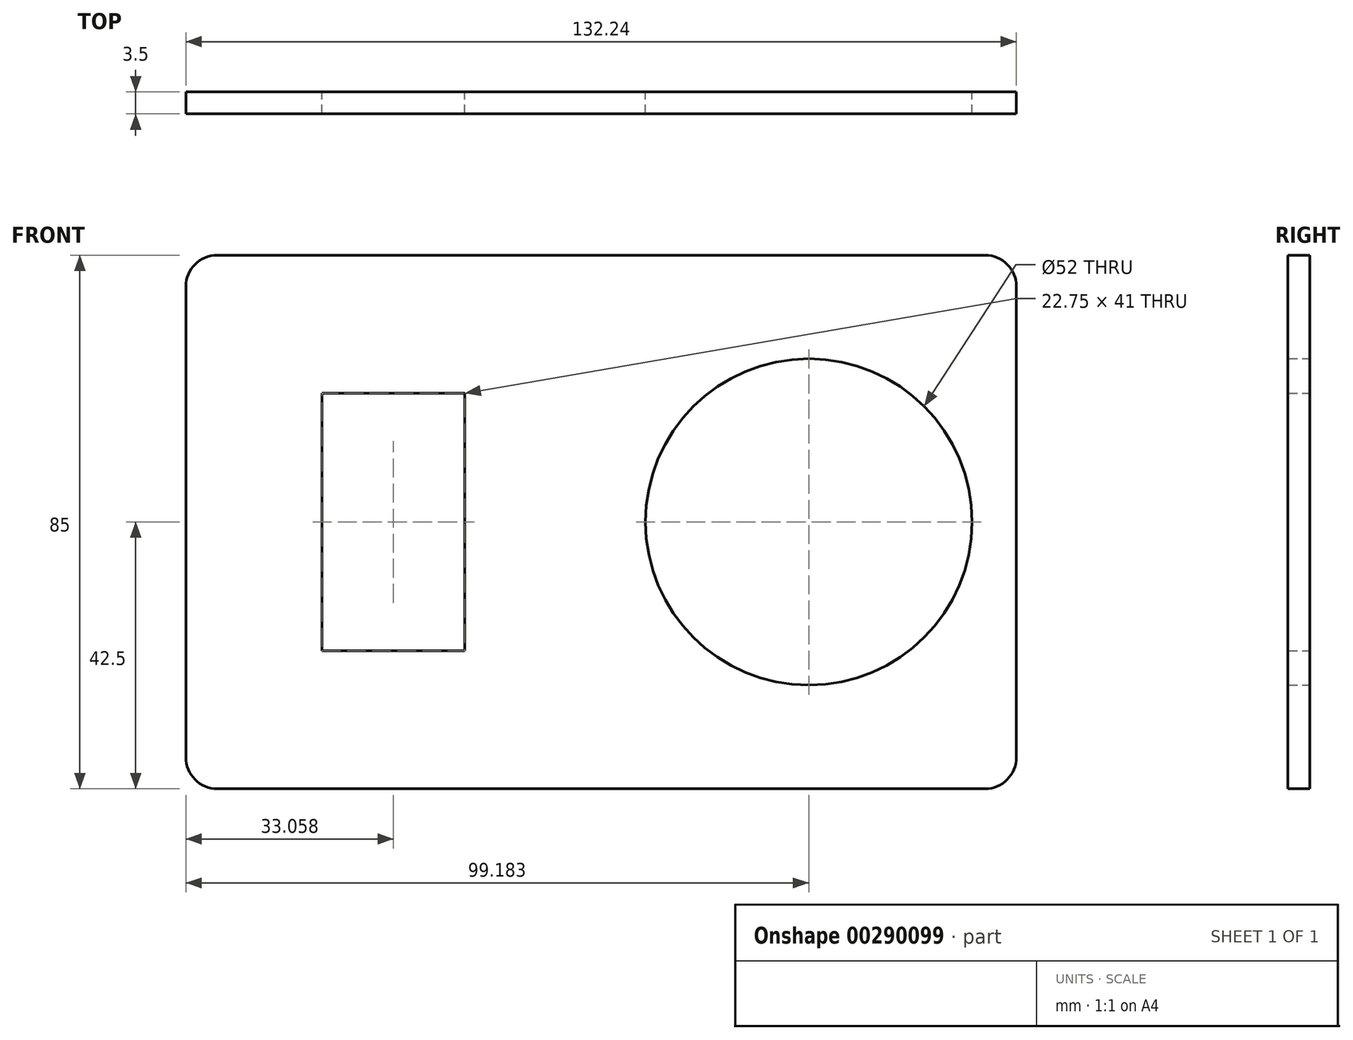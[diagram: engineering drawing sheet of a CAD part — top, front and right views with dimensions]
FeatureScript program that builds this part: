
annotation { "Feature Type Name" : "Feature", "Feature Type Description" : "" }
export const myFeature = defineFeature(function(context is Context, id is Id, definition is map)
    precondition{}
    {
        {
            var Q0;
            Q0=qCreatedBy(makeId("Front.planeOp"),FACE);
            var sketch = newSketch(context, id + "F0", { "sketchPlane" : qUnion([Q0])});
            skLineSegment(sketch, "E0.bottom", {"start": v(61.13, -42.5) * mm, "end": v(-61.12, -42.5) * mm});
            skLineSegment(sketch, "E0.top", {"start": v(61.12, 42.5) * mm, "end": v(-61.12, 42.5) * mm});
            skLineSegment(sketch, "E0.left", {"start": v(66.12, -37.5) * mm, "end": v(66.12, 37.5) * mm});
            skLineSegment(sketch, "E0.right", {"start": v(-66.12, -37.5) * mm, "end": v(-66.12, 37.5) * mm});
            skPoint(sketch, "E0.middle", {"position": v(0, 0) * mm});
            skPoint(sketch, "E1", {"position": v(-33.06, 0) * mm});
            skPoint(sketch, "E2", {"position": v(33.06, 0) * mm});
            skLineSegment(sketch, "E3.bottom", {"start": v(-21.69, -20.5) * mm, "end": v(-44.44, -20.5) * mm});
            skLineSegment(sketch, "E3.top", {"start": v(-21.69, 20.5) * mm, "end": v(-44.44, 20.5) * mm});
            skLineSegment(sketch, "E3.left", {"start": v(-21.69, -20.5) * mm, "end": v(-21.69, 20.5) * mm});
            skLineSegment(sketch, "E3.right", {"start": v(-44.44, -20.5) * mm, "end": v(-44.44, 20.5) * mm});
            skCircle(sketch, "E4", {"center": v(33.06, 0) * mm, "radius": 26 * mm});
            skPoint(sketch, "E5.visualSharp", {"position": v(-66.12, 42.5) * mm});
            skArc(sketch, "E5.filletArc", {"start": v(-61.12, 42.5) * mm, "mid": v(-64.66, 41.04) * mm, "end": v(-66.12, 37.5) * mm});
            skPoint(sketch, "E6.visualSharp", {"position": v(-66.12, -42.5) * mm});
            skArc(sketch, "E6.filletArc", {"start": v(-66.12, -37.5) * mm, "mid": v(-64.66, -41.04) * mm, "end": v(-61.12, -42.5) * mm});
            skPoint(sketch, "E7.visualSharp", {"position": v(66.12, 42.5) * mm});
            skArc(sketch, "E7.filletArc", {"start": v(66.12, 37.5) * mm, "mid": v(64.66, 41.04) * mm, "end": v(61.12, 42.5) * mm});
            skPoint(sketch, "E8.visualSharp", {"position": v(66.12, -42.5) * mm});
            skArc(sketch, "E8.filletArc", {"start": v(61.13, -42.5) * mm, "mid": v(64.66, -41.04) * mm, "end": v(66.12, -37.5) * mm});
            skPoint(sketch, "E9.start.orphan", {"position": v(-66.12, 0) * mm});
            skPoint(sketch, "E10.trimOffspring.end.orphan", {"position": v(66.12, 0) * mm});
            skPoint(sketch, "E11.orphan", {"position": v(0, 42.5) * mm});
            skPoint(sketch, "E12.end.orphan", {"position": v(0, -42.5) * mm});
            skSolve(sketch);
        }
        {
            var Q0;
            Q0=makeQuery(id+"F0.imprint","IMPRINT",FACE,{"disambiguationData":[TD([[makeQuery(id+"F0.imprint","IMPRINT",EDGE,{"derivedFrom":sQuery(id+"F0.wireOp",EDGE,"E0.bottom")}),-1.0]])]});
            extrude(context, id + "F1", {"entities" : qUnion([Q0]), "depth" : 3.5 * mm});
        }
    });
